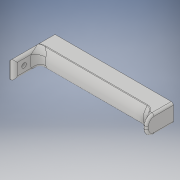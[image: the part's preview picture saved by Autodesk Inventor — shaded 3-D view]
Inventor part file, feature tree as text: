
AUTODESK INVENTOR PART (.ipt)
format: ipt  version: 2018 (Build 220112000, 112)  size: 284,160 bytes
history: native  units: in
note: dims shown in document units (in); Inventor stores cm internally (conversion verified against a paired STEP export)
features: extrude x5, fillet x5, sketch x5, chamfer x1
ambient origin geometry x8: Origin, YZ Plane, XZ Plane, XY Plane, X Axis, Y Axis, Z Axis, Center Point
bodies: Solid1 (feature_tree)
feature tree (16):
  extrude  "Extrusion1"  Depth=0.5512in
  extrude  "Extrusion2"  Depth=4.1339in TaperAngle=0.0deg
  fillet  "Fillet3"  Radius=1.5748in
  fillet  "Fillet4"  Radius=0.1575in
  extrude  "Extrusion3"  Depth=0.2756in
  extrude  "Extrusion4"  Depth=0.1575in TaperAngle=0.0deg
  fillet  "Fillet5"  Radius=0.9843in
  fillet  "Fillet6"  Radius=0.1181in
  fillet  "Fillet7"  Radius=0.2756in
  extrude  "Extrusion5"  Depth=0.0394in
  chamfer  "Chamfer1"  Distance=0.1969in
  sketch  "Sketch1"  dims[d1=0.6693in d2=0.5512in]
  sketch  "Sketch2"  dims[d3=0.4331in d4=4.1339in d5=0.0in d6=1.5748in d7=0.1575in d8=0.0in]
  sketch  "Sketch3"  dims[d11=0.1181in d12=0.2756in]
  sketch  "Sketch4"  dims[d13=0.1654in d14=0.1575in d15=0.0in d16=0.9843in d17=0.1181in d18=0.0in d19=0.2756in]
  sketch  "Sketch5"  dims[d20=0.0787in d21=0.0394in d22=0.1969in d23=0.3937in d24=0.1181in d25=0.0in d26=0.0787in d27=0.0787in d28=45.0deg]
